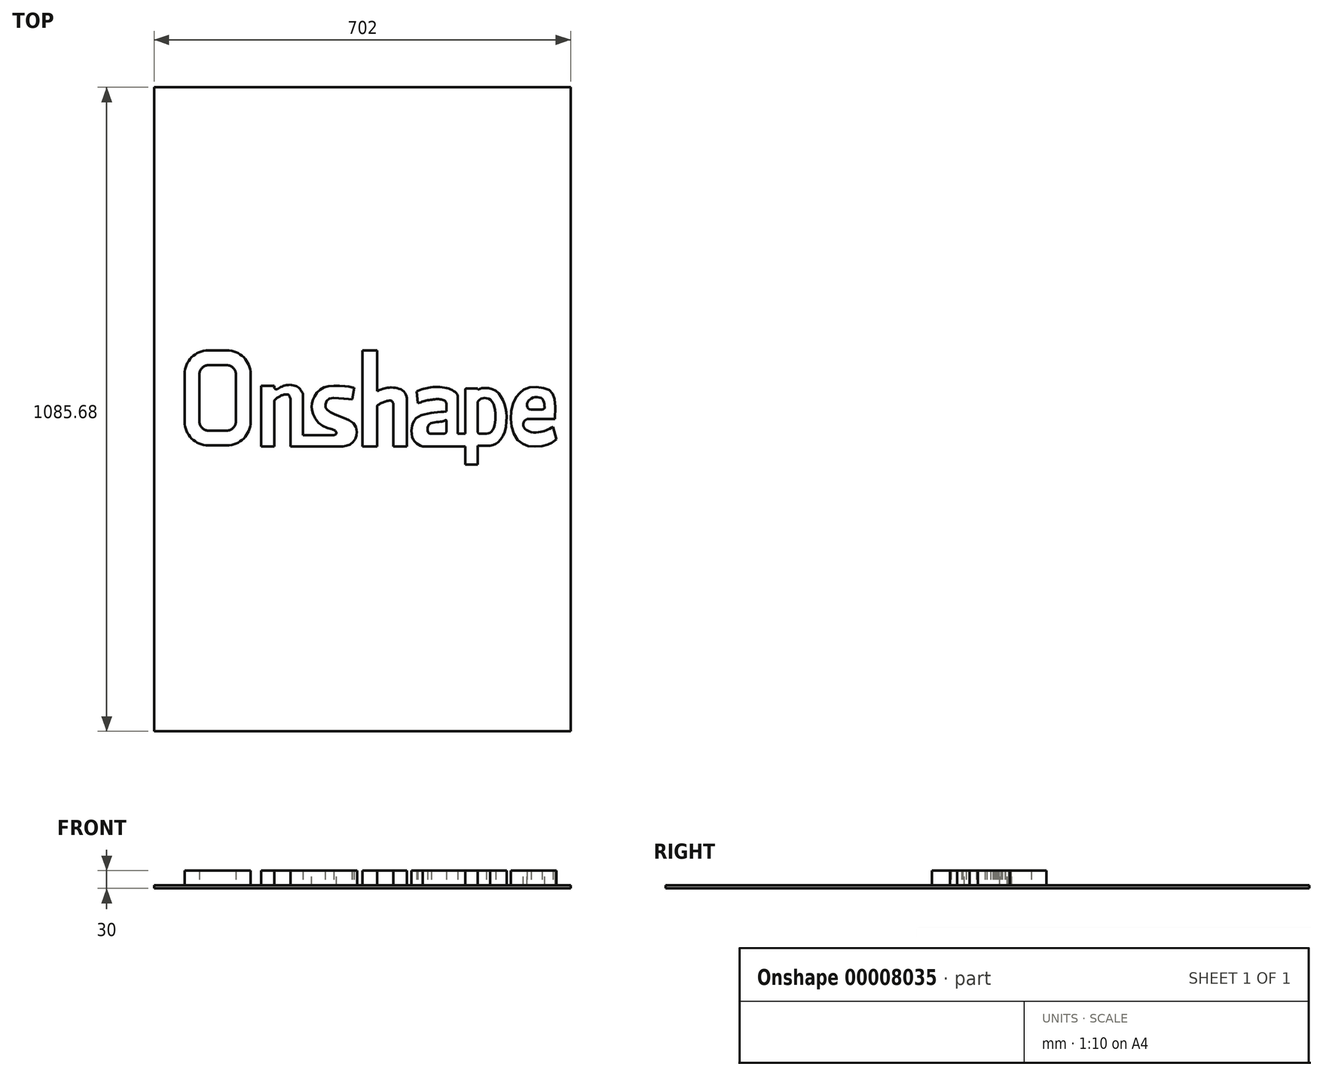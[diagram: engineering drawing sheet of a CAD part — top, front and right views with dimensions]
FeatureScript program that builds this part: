
annotation { "Feature Type Name" : "Feature", "Feature Type Description" : "" }
export const myFeature = defineFeature(function(context is Context, id is Id, definition is map)
    precondition{}
    {
        {
            var Q0;
            Q0=qCreatedBy(makeId("Top.planeOp"),FACE);
            var sketch = newSketch(context, id + "F0", { "sketchPlane" : qUnion([Q0])});
            skLineSegment(sketch, "E0.bottom", {"start": v(-351, 542.84) * mm, "end": v(351, 542.84) * mm});
            skLineSegment(sketch, "E0.top", {"start": v(-351, -542.84) * mm, "end": v(351, -542.84) * mm});
            skLineSegment(sketch, "E0.left", {"start": v(-351, 542.84) * mm, "end": v(-351, -542.84) * mm});
            skLineSegment(sketch, "E0.right", {"start": v(351, 542.84) * mm, "end": v(351, -542.84) * mm});
            skLineSegment(sketch, "E1", {"start": v(0, 0) * mm, "end": v(285.59, 0) * mm, "construction": true});
            skLineSegment(sketch, "E2", {"start": v(0, 0) * mm, "end": v(0, 273.23) * mm, "construction": true});
            skPoint(sketch, "E3", {"position": v(351, 0) * mm});
            skPoint(sketch, "E4", {"position": v(0, 542.84) * mm});
            skSolve(sketch);
        }
        {
            var Q0;
            Q0=makeQuery(id+"F0.imprint","IMPRINT",FACE,{"disambiguationData":[TD([[makeQuery(id+"F0.imprint","IMPRINT",EDGE,{"derivedFrom":sQuery(id+"F0.wireOp",EDGE,"E0.bottom")}),-1.0]])]});
            extrude(context, id + "F1", {"entities" : qUnion([Q0]), "depth" : 5 * mm});
        }
        {
            var Q0;
            Q0=makeQuery(id+"F1.opExtrude","CAP_FACE",FACE,{"disambiguationData":[OSD([sQuery(id+"F0.wireOp",EDGE,"E0.bottom"),sQuery(id+"F0.wireOp",EDGE,"E0.top"),sQuery(id+"F0.wireOp",EDGE,"E0.left"),sQuery(id+"F0.wireOp",EDGE,"E0.right")])],"isStart":false});
            var sketch = newSketch(context, id + "F2", { "sketchPlane" : qUnion([Q0])});
            skLineSegment(sketch, "E5", {"start": v(-299.7, 59.23) * mm, "end": v(-299.7, -20.92) * mm});
            skLineSegment(sketch, "E6", {"start": v(-259.7, -60.92) * mm, "end": v(-228.47, -60.92) * mm});
            skLineSegment(sketch, "E7", {"start": v(-188.47, -20.92) * mm, "end": v(-188.47, 59.23) * mm});
            skLineSegment(sketch, "E8", {"start": v(-228.47, 99.23) * mm, "end": v(-259.7, 99.23) * mm});
            skPoint(sketch, "E9.visualSharp", {"position": v(-299.7, -60.92) * mm});
            skArc(sketch, "E9.filletArc", {"start": v(-299.7, -20.92) * mm, "mid": v(-287.98, -49.2) * mm, "end": v(-259.7, -60.92) * mm});
            skPoint(sketch, "E10.visualSharp", {"position": v(-188.47, -60.92) * mm});
            skArc(sketch, "E10.filletArc", {"start": v(-228.47, -60.92) * mm, "mid": v(-200.19, -49.2) * mm, "end": v(-188.47, -20.92) * mm});
            skPoint(sketch, "E11.visualSharp", {"position": v(-299.7, 99.23) * mm});
            skArc(sketch, "E11.filletArc", {"start": v(-259.7, 99.23) * mm, "mid": v(-287.98, 87.51) * mm, "end": v(-299.7, 59.23) * mm});
            skPoint(sketch, "E12.visualSharp", {"position": v(-188.47, 99.23) * mm});
            skArc(sketch, "E12.filletArc", {"start": v(-188.47, 59.23) * mm, "mid": v(-200.19, 87.51) * mm, "end": v(-228.47, 99.23) * mm});
            skArc(sketch, "E13.0", {"start": v(-259.7, 74.23) * mm, "mid": v(-270.3, 69.83) * mm, "end": v(-274.7, 59.23) * mm});
            skLineSegment(sketch, "E13.1", {"start": v(-228.47, 74.23) * mm, "end": v(-259.7, 74.23) * mm});
            skArc(sketch, "E13.2", {"start": v(-213.47, 59.23) * mm, "mid": v(-217.87, 69.83) * mm, "end": v(-228.47, 74.23) * mm});
            skLineSegment(sketch, "E13.3", {"start": v(-213.47, -20.92) * mm, "end": v(-213.47, 59.23) * mm});
            skArc(sketch, "E13.4", {"start": v(-228.47, -35.92) * mm, "mid": v(-217.87, -31.52) * mm, "end": v(-213.47, -20.92) * mm});
            skLineSegment(sketch, "E13.5", {"start": v(-274.7, 59.23) * mm, "end": v(-274.7, -20.92) * mm});
            skLineSegment(sketch, "E13.6", {"start": v(-259.7, -35.92) * mm, "end": v(-228.47, -35.92) * mm});
            skArc(sketch, "E13.7", {"start": v(-274.7, -20.92) * mm, "mid": v(-270.3, -31.52) * mm, "end": v(-259.7, -35.92) * mm});
            skLineSegment(sketch, "E14", {"start": v(-170.45, -62.44) * mm, "end": v(-170.45, 39.68) * mm});
            skLineSegment(sketch, "E15", {"start": v(-170.45, 39.68) * mm, "end": v(-148.72, 39.68) * mm});
            skLineSegment(sketch, "E16", {"start": v(-148.72, 39.68) * mm, "end": v(-148.72, 37.04) * mm});
            skLineSegment(sketch, "E17", {"start": v(-148.72, -62.44) * mm, "end": v(-170.45, -62.44) * mm});
            skLineSegment(sketch, "E18", {"start": v(-121.4, 17.58) * mm, "end": v(-121.4, -62.44) * mm});
            skLineSegment(sketch, "E19", {"start": v(-121.4, -62.44) * mm, "end": v(-48.13, -62.44) * mm});
            skLineSegment(sketch, "E20", {"start": v(-48.13, -43.6) * mm, "end": v(-100.29, -43.6) * mm});
            skLineSegment(sketch, "E21", {"start": v(-100.29, -43.6) * mm, "end": v(-100.29, 25.35) * mm});
            skFitSpline(sketch, "E22", {"points": [v(-148.72, 14.77) * mm, v(-138.78, 22.22) * mm, v(-125.75, 24.7) * mm, v(-121.4, 18.5) * mm], "startDerivative": vector(24.47, 22.54) * mm, "endDerivative": vector(10.61, -28.3) * mm});
            skFitSpline(sketch, "E23", {"points": [v(-148.72, 36.08) * mm, v(-146.57, 33.73) * mm, v(-143.96, 33.73) * mm, v(-137.44, 37.38) * mm, v(-127.78, 40.78) * mm, v(-114.46, 40) * mm, v(-106.37, 35.3) * mm, v(-100.29, 26.76) * mm], "startDerivative": vector(21.71, -30.96) * mm, "endDerivative": vector(33.67, -55.34) * mm});
            skLineSegment(sketch, "E24.trimOffspring", {"start": v(-148.72, 12.57) * mm, "end": v(-148.72, -62.44) * mm});
            skFitSpline(sketch, "E25", {"points": [v(-48.13, -43.6) * mm, v(-44.9, -42.6) * mm, v(-43.7, -40.64) * mm, v(-45.58, -36.09) * mm, v(-57.63, -32.04) * mm, v(-75.73, -20.85) * mm, v(-84.33, -3.82) * mm, v(-85.46, 5.7) * mm, v(-84.17, 13.46) * mm, v(-78.2, 26.16) * mm, v(-66.3, 36) * mm, v(-48.13, 39.37) * mm, v(-25.89, 38.59) * mm, v(-17.86, 37.03) * mm], "startDerivative": vector(84.75, 14.56) * mm, "endDerivative": vector(103.74, -25.5) * mm});
            skLineSegment(sketch, "E26", {"start": v(-48.13, -62.44) * mm, "end": v(-32.73, -62.44) * mm});
            skFitSpline(sketch, "E27", {"points": [v(-32.73, -62.44) * mm, v(-21.15, -59.62) * mm, v(-12.78, -51.3) * mm, v(-9.11, -40.31) * mm, v(-14.98, -23.83) * mm, v(-38.05, -12.1) * mm, v(-54.17, -4.42) * mm, v(-61.86, 2.18) * mm, v(-61.5, 11.7) * mm, v(-54.17, 18.3) * mm, v(-32.73, 17.93) * mm, v(-17.17, 16.46) * mm], "startDerivative": vector(97.21, 0) * mm, "endDerivative": vector(103.18, -17.03) * mm});
            skLineSegment(sketch, "E28", {"start": v(-17.17, 16.46) * mm, "end": v(-13.93, 36.16) * mm});
            skLineSegment(sketch, "E29", {"start": v(-13.93, 36.16) * mm, "end": v(-17.86, 37.03) * mm});
            skLineSegment(sketch, "E30", {"start": v(-0.12, -62.44) * mm, "end": v(-0.12, 99.47) * mm});
            skLineSegment(sketch, "E31", {"start": v(-0.12, 99.47) * mm, "end": v(24.62, 99.47) * mm});
            skLineSegment(sketch, "E32", {"start": v(24.62, 99.47) * mm, "end": v(24.62, 30.35) * mm});
            skLineSegment(sketch, "E33", {"start": v(24.62, -62.44) * mm, "end": v(-0.12, -62.44) * mm});
            skLineSegment(sketch, "E34", {"start": v(52.3, -62.44) * mm, "end": v(52.3, 9.6) * mm});
            skLineSegment(sketch, "E35", {"start": v(74.9, 12.38) * mm, "end": v(74.9, -62.44) * mm});
            skLineSegment(sketch, "E36", {"start": v(74.9, -62.44) * mm, "end": v(52.3, -62.44) * mm});
            skFitSpline(sketch, "E37", {"points": [v(24.62, 5.44) * mm, v(27.86, 8.13) * mm, v(34.95, 11.8) * mm, v(43.26, 14.24) * mm, v(49.13, 14) * mm, v(51.82, 10.75) * mm, v(52.3, 8.38) * mm], "startDerivative": vector(19.33, 17.96) * mm, "endDerivative": vector(0, -32.88) * mm});
            skFitSpline(sketch, "E38", {"points": [v(24.62, 30.35) * mm, v(29.1, 32.6) * mm, v(36.01, 34.84) * mm, v(42.58, 36.4) * mm, v(53.13, 36.4) * mm, v(62.46, 34.5) * mm, v(70.24, 29.66) * mm, v(74.22, 22.05) * mm, v(74.9, 15.3) * mm, v(74.9, 12.38) * mm], "startDerivative": vector(44.62, 25.05) * mm, "endDerivative": vector(-0.44, -37.07) * mm});
            skLineSegment(sketch, "E39.trimOffspring", {"start": v(24.62, 5.44) * mm, "end": v(24.62, -62.44) * mm});
            skFitSpline(sketch, "E40", {"points": [v(91.47, 29.81) * mm, v(100.87, 33.76) * mm, v(109.8, 36) * mm, v(121.47, 37.76) * mm, v(137.6, 36.75) * mm, v(148.95, 33.38) * mm, v(156.51, 28.8) * mm, v(160.7, 22.33) * mm], "startDerivative": vector(46.04, 27.08) * mm, "endDerivative": vector(2.85, -63.73) * mm});
            skLineSegment(sketch, "E41", {"start": v(160.7, 22.33) * mm, "end": v(160.7, -41.26) * mm});
            skLineSegment(sketch, "E42", {"start": v(101.8, -62.44) * mm, "end": v(173.45, -62.44) * mm});
            skFitSpline(sketch, "E43", {"points": [v(101.8, -62.44) * mm, v(94.97, -60.1) * mm, v(89.25, -55.3) * mm, v(84.04, -47.25) * mm, v(82.98, -33.71) * mm, v(84.45, -25.96) * mm, v(89.86, -15.84) * mm, v(100.35, -9.98) * mm, v(114.96, -6.23) * mm, v(130.08, -4.58) * mm, v(141.68, -3.82) * mm], "startDerivative": vector(-83.06, 22.5) * mm, "endDerivative": vector(90.2, 15.78) * mm});
            skLineSegment(sketch, "E44", {"start": v(141.68, -3.82) * mm, "end": v(141.68, 9.14) * mm});
            skLineSegment(sketch, "E45", {"start": v(91.47, 29.81) * mm, "end": v(93.14, 10.22) * mm});
            skFitSpline(sketch, "E46", {"points": [v(93.14, 10.22) * mm, v(102.54, 13.17) * mm, v(110.48, 15.2) * mm, v(119.18, 16.47) * mm, v(126.74, 17.06) * mm, v(133.29, 16.56) * mm, v(138.37, 14.63) * mm, v(141.68, 9.14) * mm], "startDerivative": vector(58.12, 18.51) * mm, "endDerivative": vector(-2.77, -59.3) * mm});
            skLineSegment(sketch, "E47", {"start": v(141.68, -18.9) * mm, "end": v(141.68, -36.46) * mm});
            skLineSegment(sketch, "E48", {"start": v(116.36, -41.46) * mm, "end": v(136.68, -41.46) * mm});
            skFitSpline(sketch, "E49", {"points": [v(116.36, -41.46) * mm, v(112.4, -40.43) * mm, v(110.68, -38.46) * mm, v(109.69, -34.27) * mm, v(110.68, -28.76) * mm, v(114.38, -24.32) * mm, v(123.1, -21.93) * mm, v(132.88, -20.86) * mm, v(136.9, -19.71) * mm, v(139.17, -18.9) * mm, v(140.44, -18.15) * mm, v(141.3, -18.44) * mm, v(141.68, -18.9) * mm], "startDerivative": vector(-49.56, 8.3) * mm, "endDerivative": vector(5.14, -15.4) * mm});
            skLineSegment(sketch, "E50", {"start": v(160.7, -41.26) * mm, "end": v(173.45, -41.26) * mm});
            skLineSegment(sketch, "E51", {"start": v(173.45, -41.26) * mm, "end": v(173.45, 33.12) * mm});
            skLineSegment(sketch, "E52", {"start": v(173.45, -62.44) * mm, "end": v(173.45, -93.45) * mm});
            skLineSegment(sketch, "E53", {"start": v(173.45, -93.45) * mm, "end": v(194.65, -93.45) * mm});
            skLineSegment(sketch, "E54", {"start": v(194.65, -93.45) * mm, "end": v(194.65, -61.56) * mm});
            skLineSegment(sketch, "E55", {"start": v(194.65, -61.56) * mm, "end": v(215.6, -61.56) * mm});
            skLineSegment(sketch, "E56", {"start": v(194.65, -38.26) * mm, "end": v(194.65, 12.53) * mm});
            skLineSegment(sketch, "E57", {"start": v(175.45, 35.12) * mm, "end": v(194.65, 35.12) * mm});
            skLineSegment(sketch, "E58", {"start": v(197.65, -41.26) * mm, "end": v(209.14, -41.26) * mm});
            skFitSpline(sketch, "E59", {"points": [v(194.65, 12.53) * mm, v(197.22, 15.65) * mm, v(199.78, 17.28) * mm, v(203.26, 18.68) * mm, v(208.38, 18.9) * mm, v(214.66, 16.82) * mm, v(220.24, 10.54) * mm, v(224.2, -3.65) * mm, v(224.2, -18.53) * mm, v(222.34, -29.23) * mm, v(217.92, -37.6) * mm, v(213.5, -40.4) * mm, v(209.14, -41.26) * mm], "startDerivative": vector(39.46, 54.88) * mm, "endDerivative": vector(-66.44, -9.1) * mm});
            skFitSpline(sketch, "E60", {"points": [v(194.65, 35.12) * mm, v(194.65, 34.24) * mm, v(195.2, 33.45) * mm, v(197.3, 33.82) * mm, v(200.08, 35.12) * mm, v(204.76, 35.8) * mm, v(215.73, 35.12) * mm, v(226.27, 30.15) * mm, v(232.85, 22.81) * mm, v(239.05, 10.48) * mm, v(242.37, -1.64) * mm, v(243.18, -18.11) * mm, v(240.18, -36.82) * mm, v(233.54, -50.2) * mm, v(226.74, -57.3) * mm, v(221.64, -59.78) * mm, v(215.6, -61.56) * mm], "startDerivative": vector(-4.32, -40.56) * mm, "endDerivative": vector(-113.2, -25.5) * mm});
            skPoint(sketch, "E61.orphan", {"position": v(160.7, 22.88) * mm});
            skFitSpline(sketch, "E62", {"points": [v(326.96, -50.83) * mm, v(320.02, -56.08) * mm, v(315.24, -58.6) * mm, v(309.1, -60.81) * mm, v(299.72, -62.54) * mm, v(285.17, -62.73) * mm, v(276.37, -60.93) * mm, v(268.48, -56.75) * mm, v(259.32, -48.7) * mm, v(253.39, -35.65) * mm, v(250.61, -20.8) * mm, v(250.93, -3.85) * mm, v(254.2, 10.02) * mm, v(259.94, 21.4) * mm, v(265.37, 27.44) * mm, v(270.42, 32.05) * mm, v(278.77, 36) * mm, v(290.84, 37.54) * mm, v(303.57, 36.22) * mm, v(313.45, 33.15) * mm, v(318.72, 29.2) * mm, v(322.67, 21.95) * mm, v(324.64, 13.83) * mm, v(324.86, -16.25) * mm], "startDerivative": vector(-94.33, -93.91) * mm, "endDerivative": vector(-10.07, -512.06) * mm});
            skLineSegment(sketch, "E63", {"start": v(324.86, -16.25) * mm, "end": v(277.89, -16.25) * mm});
            skFitSpline(sketch, "E64", {"points": [v(277.89, -16.25) * mm, v(273.27, -19.98) * mm, v(271.31, -24.74) * mm, v(271.72, -28.5) * mm, v(273.39, -32) * mm, v(276.36, -34.76) * mm, v(281.36, -37.5) * mm, v(290.54, -39.2) * mm, v(302.45, -37.83) * mm, v(308.36, -35.97) * mm, v(315.28, -32.97) * mm, v(321.28, -29.83) * mm], "startDerivative": vector(-38.92, -19.1) * mm, "endDerivative": vector(57.68, 31.07) * mm});
            skLineSegment(sketch, "E65", {"start": v(321.28, -29.83) * mm, "end": v(326.96, -50.83) * mm});
            skLineSegment(sketch, "E66", {"start": v(284.38, -0.68) * mm, "end": v(303.3, -0.68) * mm});
            skFitSpline(sketch, "E67", {"points": [v(303.3, -0.68) * mm, v(305.2, -0.1) * mm, v(306.86, 1.74) * mm, v(307.15, 5.36) * mm, v(306.8, 10.1) * mm, v(304.71, 15.56) * mm, v(301.1, 19.05) * mm, v(295.06, 20.33) * mm, v(287.73, 19.63) * mm, v(282.73, 16.6) * mm, v(279.6, 13.57) * mm, v(277.7, 8.85) * mm, v(278.01, 3.51) * mm, v(280.22, 0.9) * mm, v(284.38, -0.68) * mm], "startDerivative": vector(39.67, 11.95) * mm, "endDerivative": vector(102.32, -7.72) * mm});
            skArc(sketch, "E68.filletArc", {"start": v(194.65, -38.26) * mm, "mid": v(195.53, -40.38) * mm, "end": v(197.65, -41.26) * mm});
            skLineSegment(sketch, "E69.extension", {"start": v(-148.12, 35.24) * mm, "end": v(-148.12, 35.24) * mm});
            skArc(sketch, "E70.filletArc", {"start": v(-148.72, 37.04) * mm, "mid": v(-148.57, 36.1) * mm, "end": v(-148.12, 35.24) * mm});
            skArc(sketch, "E71.filletArc", {"start": v(136.68, -41.46) * mm, "mid": v(140.22, -40) * mm, "end": v(141.68, -36.46) * mm});
            skLineSegment(sketch, "E72.extension", {"start": v(-147.06, 16.28) * mm, "end": v(-147.06, 16.28) * mm});
            skArc(sketch, "E73.filletArc", {"start": v(-147.06, 16.28) * mm, "mid": v(-148.29, 14.6) * mm, "end": v(-148.72, 12.57) * mm});
            skArc(sketch, "E74.filletArc", {"start": v(-100.29, 25.35) * mm, "mid": v(-100.48, 26.71) * mm, "end": v(-101.03, 27.97) * mm});
            skArc(sketch, "E75.filletArc", {"start": v(-121.4, 17.58) * mm, "mid": v(-121.48, 18.5) * mm, "end": v(-121.73, 19.38) * mm});
            skArc(sketch, "E76.filletArc", {"start": v(175.45, 35.12) * mm, "mid": v(174.04, 34.54) * mm, "end": v(173.45, 33.12) * mm});
            skSolve(sketch);
        }
        {
            var Q0;
            {Q0=qUnion([makeQuery(id+"F2.imprint","IMPRINT",FACE,{"disambiguationData":[TD([[makeQuery(id+"F2.imprint","IMPRINT",EDGE,{"derivedFrom":sQuery(id+"F2.wireOp",EDGE,"E14")}),-1.0]])]}),makeQuery(id+"F2.imprint","IMPRINT",FACE,{"disambiguationData":[TD([[makeQuery(id+"F2.imprint","IMPRINT",EDGE,{"derivedFrom":sQuery(id+"F2.wireOp",EDGE,"E30")}),-1.0]])]}),makeQuery(id+"F2.imprint","IMPRINT",FACE,{"disambiguationData":[TD([[makeQuery(id+"F2.imprint","IMPRINT",EDGE,{"derivedFrom":sQuery(id+"F2.wireOp",EDGE,"E5")}),1.0]])]}),makeQuery(id+"F2.imprint","IMPRINT",FACE,{"disambiguationData":[TD([[makeQuery(id+"F2.imprint","IMPRINT",EDGE,{"derivedFrom":sQuery(id+"F2.wireOp",EDGE,"E62")}),-1.0]])]}),makeQuery(id+"F2.imprint","IMPRINT",FACE,{"disambiguationData":[TD([[makeQuery(id+"F2.imprint","IMPRINT",EDGE,{"derivedFrom":sQuery(id+"F2.wireOp",EDGE,"E40")}),-1.0]])]})]);}
            extrude(context, id + "F3", {"entities" : qUnion([Q0]), "operationType" : NewBodyOperationType.ADD, "depth" : 25 * mm});
        }
    });
